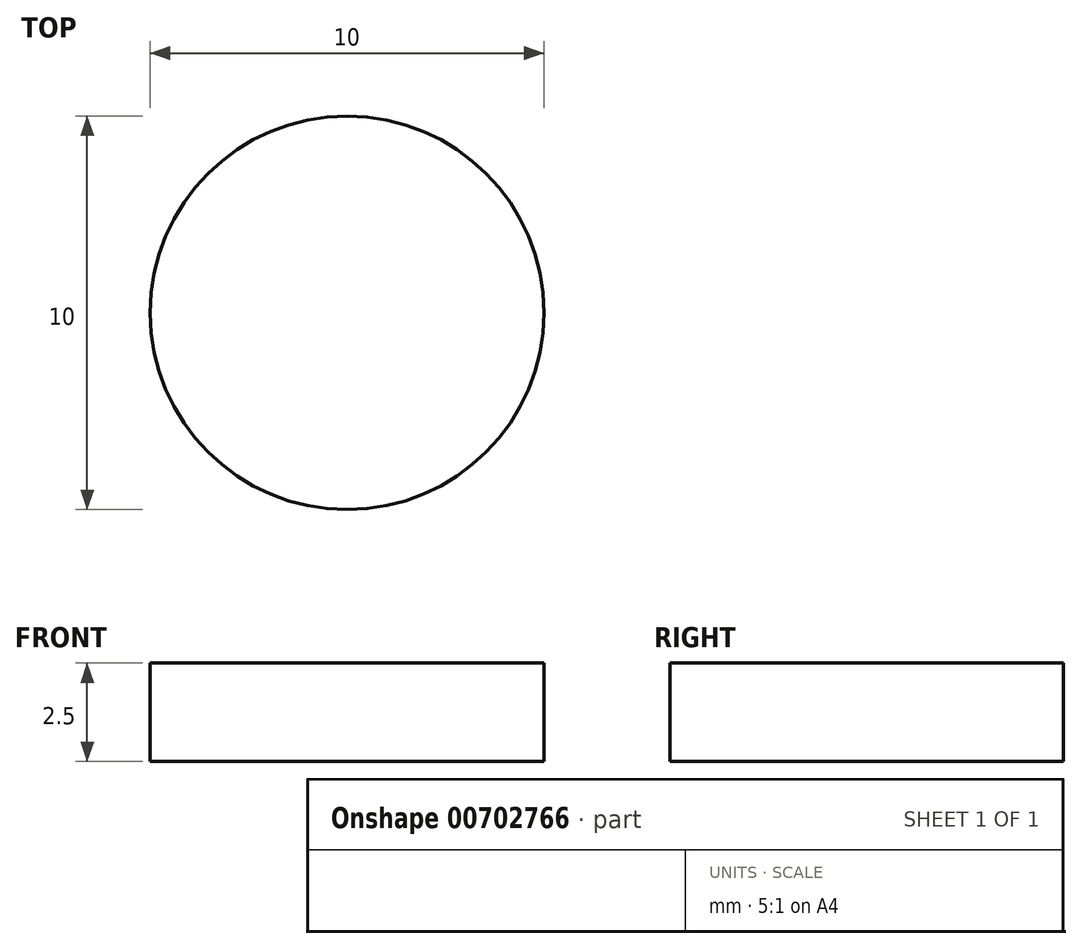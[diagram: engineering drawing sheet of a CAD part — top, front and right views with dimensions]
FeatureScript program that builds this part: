
annotation { "Feature Type Name" : "Feature", "Feature Type Description" : "" }
export const myFeature = defineFeature(function(context is Context, id is Id, definition is map)
    precondition{}
    {
        {
            var Q0;
            Q0=qCreatedBy(makeId("Top.planeOp"),FACE);
            var sketch = newSketch(context, id + "F0", { "sketchPlane" : qUnion([Q0])});
            skCircle(sketch, "E0", {"center": v(0, 0) * mm, "radius": 5 * mm});
            skSolve(sketch);
        }
        {
            var Q0;
            Q0 = qSketchRegion(id + "F0", true);
            extrude(context, id + "F1", {"entities" : qUnion([Q0]), "depth" : 2.5 * mm, "offsetDistance" : 25 * mm});
        }
    });
